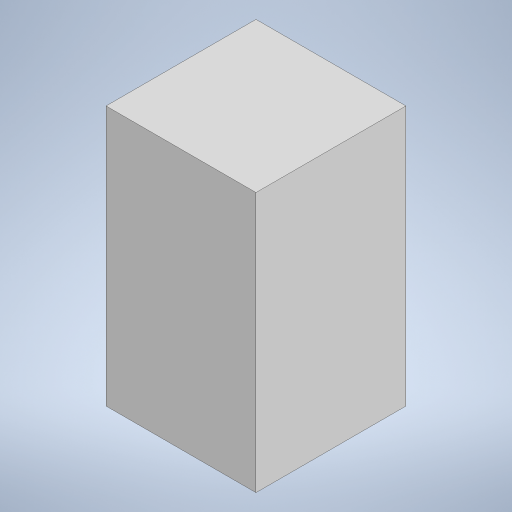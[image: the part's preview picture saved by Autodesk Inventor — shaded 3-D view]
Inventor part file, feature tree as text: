
AUTODESK INVENTOR PART (.ipt)
format: ipt  version: 2024.3 (Build 283343000, 343)  size: 167,936 bytes
history: native  units: mm
features: other x1, extrude x1, sketch x1
ambient origin geometry x8: Origin, YZ Plane, XZ Plane, XY Plane, X Axis, Y Axis, Z Axis, Center Point
bodies: Body1 (feature_tree)
feature tree (3):
  other  "ソリッド1"
  extrude  "押し出し1"  Depth=260.0mm
  sketch  "スケッチ1"
